# Revit family: Domotics-DomesticRanges-GEWISS-SYSTEM_SIGNALLING-BUZZER
name_source: partatom
category: Apparecchi elettrici
revit_build: Autodesk Revit 2016 (Build: 20161004_0715(x64)
units: mm (PartAtom-declared; Revit-internal decimal feet)

## family parameters
Condiviso = Sì
Host = Superficie
Mantenere orientamento annotazione = Sì
Numero OmniClass = 23.80.50.11.14
Punto di calcolo locali = Sì
Quota connettore circolare = Usa diametro
Taglio con vuoti quando caricato = Sì
Tipo di parte = Normale
Titolo OmniClass = Switches

## types (8) — shared parameters
Bidimensionale = bidimensionale system segnal acustica : RONZATORE
Carico apparente = 0 VA
Catalogue = DOMOTICS
Catalogue Range = SYSTEM - DOMESTIC RANGE
Electrocod = 0132
IDF = 9a98c68e-3d17-41c1-8a24-6a22314938d6
IDT = e742e08a-28ab-46fd-bce7-8d2241ef58ca
Immagine tipo = GW21620.jpg
Larghezza pulsante = 23 mm  [stored 0.0754593 ft]
N. poli = 1
No. SYSTEM modules = 1
Power input = 8VA
Produttore = GEWISS S.p.A.
Prospetto di default = 1219 mm
Simbolo = SIMBOLO SEGNAL ACUSTICA : RONZATORE
Technical sheet = https://www.gewiss.com
Tipo = SYSTEM SEGNAL ACUSTICA_BASE : GW21620 - Nero - Ronzatore - 230V
URL = https://www.gewiss.com
Version file RFA = 19.4
Volt = 230 V

## per-type parameters (varying)
| type | Colour | Description. | Descrizione | EAN code | Modello | SEO | Sound intensity | Supply voltage | Voltage |
| GW21616 - Bell-230V-50hz 8VA black | Black | Bell | BELL-230V-50HZ 8VA SY/BK | 8011564129511 | GW21616 | Ringer | 80 dB (at 1 m) | 230V ac - 50Hz | 230V ac - 50 Hz |
| GW21617 - Buzzer 12V-50hz 8VA black | Black | Buzzer | BUZZER 12V-50HZ 8VA SY/BK | 8011564129528 | GW21617 | Buzzer | 75 dB (at 1 m) | 12 V - 50 Hz | 12 V - 50 Hz |
| GW20620 - Buzzer 230V-50hz 8VA white | White | Buzzer | BUZZER 230V-50HZ 8VA SY/WT | 8011564001138 | GW20620 | Buzzer | 75 dB (at 1 m) | 230V ac - 50Hz | 230V ac - 50 Hz |
| GW20617 - Buzzer 12V-50hz 8VA white | White | Buzzer | BUZZER 12V-50HZ 8VA SY/WT | 8011564001107 | GW20617 | Buzzer | 75 dB (at 1 m) | 12V ac - 50 Hz | 12V ac - 50 Hz |
| GW21613 - Bell-12V-50hz 8VA black | Black | Bell | BELL-12V-50HZ 8VA SY/BK | 8011564129443 | GW21613 | Ringer | 80 dB (at 1 m) | 12 V - 50 Hz | 12 V - 50 Hz |
| GW21620 - Buzzer 230V-50hz 8VA black | Black | Buzzer | BUZZER 230V-50HZ 8VA SY/BK | 8011564129542 | GW21620 | Buzzer | 75 dB (at 1 m) | 230 V - 50 Hz | 230 V - 50 Hz |
| GW20616 - Bell-230V-50hz 8VA white | White | Bell | BELL-230V-50HZ 8VA SY/WT | 8011564001091 | GW20616 | Ringer | 80 dB (at 1 m) | 230V ac - 50Hz | 230V ac - 50 Hz |
| GW20613 - Bell-12V-50hz 8VA white | White | Bell | BELL-12V-50HZ 8VA SY/WT | 8011564001060 | GW20613 | Ringer | 80 dB (at 1 m) | 12 V - 50 Hz | 12 V - 50 Hz |

note: [stored X ft] marks values corroborated as IEEE doubles in the binary element streams (Revit-internal decimal feet)

## geometry (parser evidence)
native form markers: Sweep x1
no freeform markers — native parametric forms only
